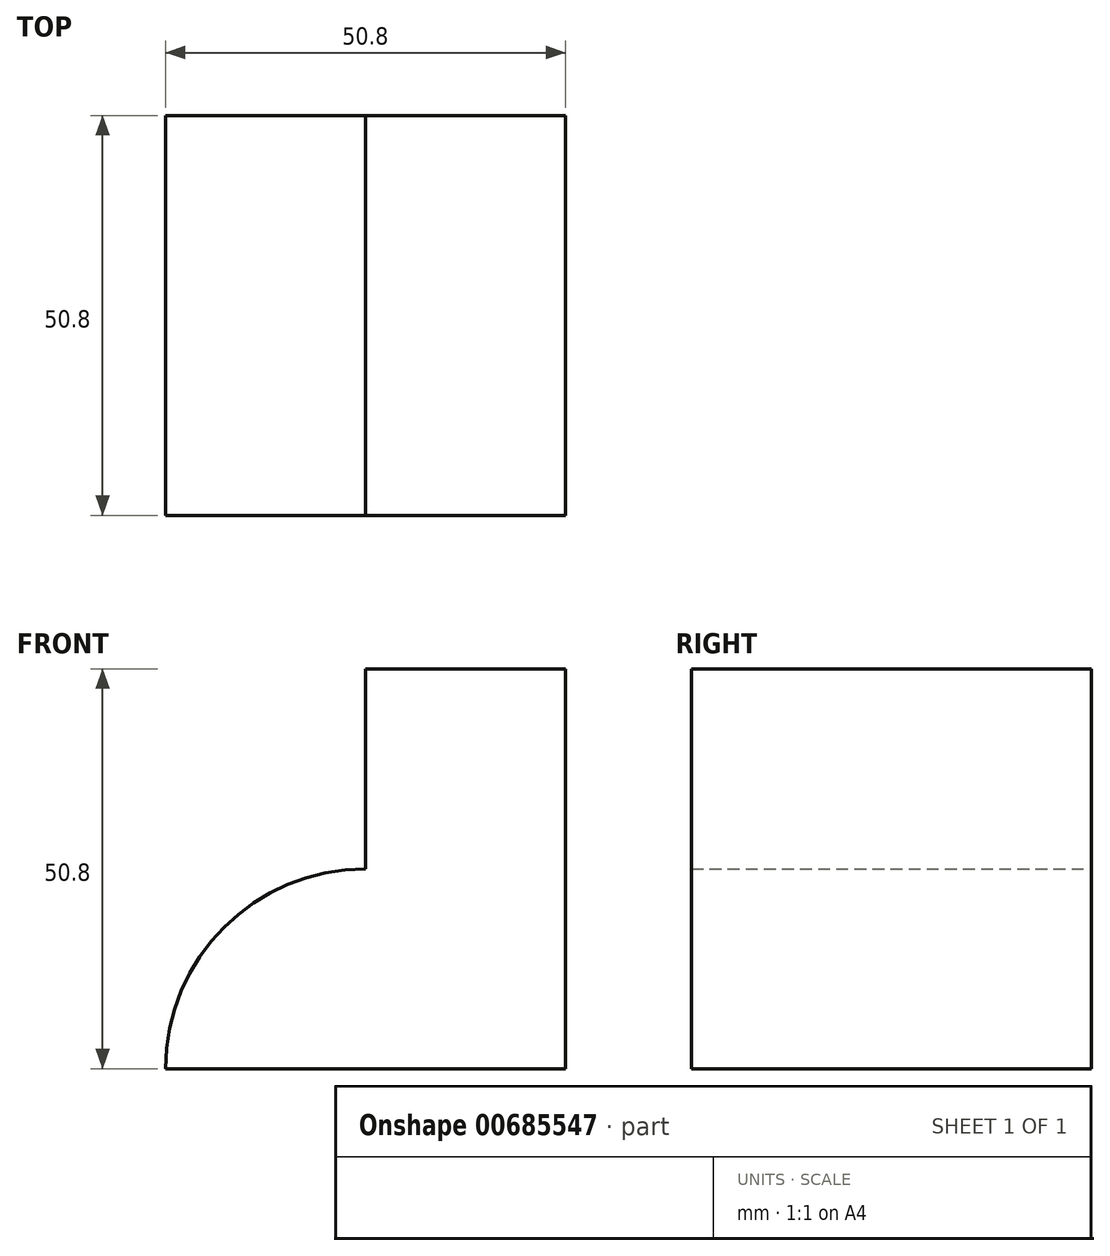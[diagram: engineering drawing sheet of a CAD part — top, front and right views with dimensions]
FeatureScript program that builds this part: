
annotation { "Feature Type Name" : "Feature", "Feature Type Description" : "" }
export const myFeature = defineFeature(function(context is Context, id is Id, definition is map)
    precondition{}
    {
        {
            var Q0;
            Q0=qCreatedBy(makeId("Front.planeOp"),FACE);
            var sketch = newSketch(context, id + "F0", { "sketchPlane" : qUnion([Q0])});
            skLineSegment(sketch, "E0", {"start": v(0, 0) * mm, "end": v(0, 50.8) * mm});
            skLineSegment(sketch, "E1", {"start": v(0, 50.8) * mm, "end": v(-25.4, 50.8) * mm});
            skLineSegment(sketch, "E2", {"start": v(-25.4, 50.8) * mm, "end": v(-25.4, 25.4) * mm});
            skLineSegment(sketch, "E3", {"start": v(0, 0) * mm, "end": v(-50.8, 0) * mm});
            skArc(sketch, "E4", {"start": v(-25.4, 25.4) * mm, "mid": v(-43.36, 17.96) * mm, "end": v(-50.8, 0) * mm});
            skSolve(sketch);
        }
        {
            var Q0;
            Q0 = qSketchRegion(id + "F0", true);
            extrude(context, id + "F1", {"entities" : qUnion([Q0]), "depth" : 50.8 * mm, "offsetDistance" : 25.4 * mm});
        }
    });
